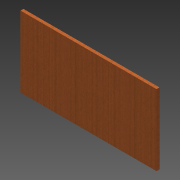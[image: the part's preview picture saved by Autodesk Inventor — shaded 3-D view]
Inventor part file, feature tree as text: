
AUTODESK INVENTOR PART (.ipt)
format: ipt  version: 2013 (Build 170138000, 138)  size: 83,968 bytes
history: native  units: in
note: dims shown in document units (in); Inventor stores cm internally (conversion verified against a paired STEP export)
features: extrude x1, sketch x1
ambient origin geometry x8: Origin, YZ Plane, XZ Plane, XY Plane, X Axis, Y Axis, Z Axis, Center Point
bodies: Solid1 (feature_tree)
feature tree (2):
  extrude  "Extrusion1"  Depth=12.0in
  sketch  "Sketch1"  dims[d0=23.0in d1=12.0in d2=0.5in d3=0.0in]
